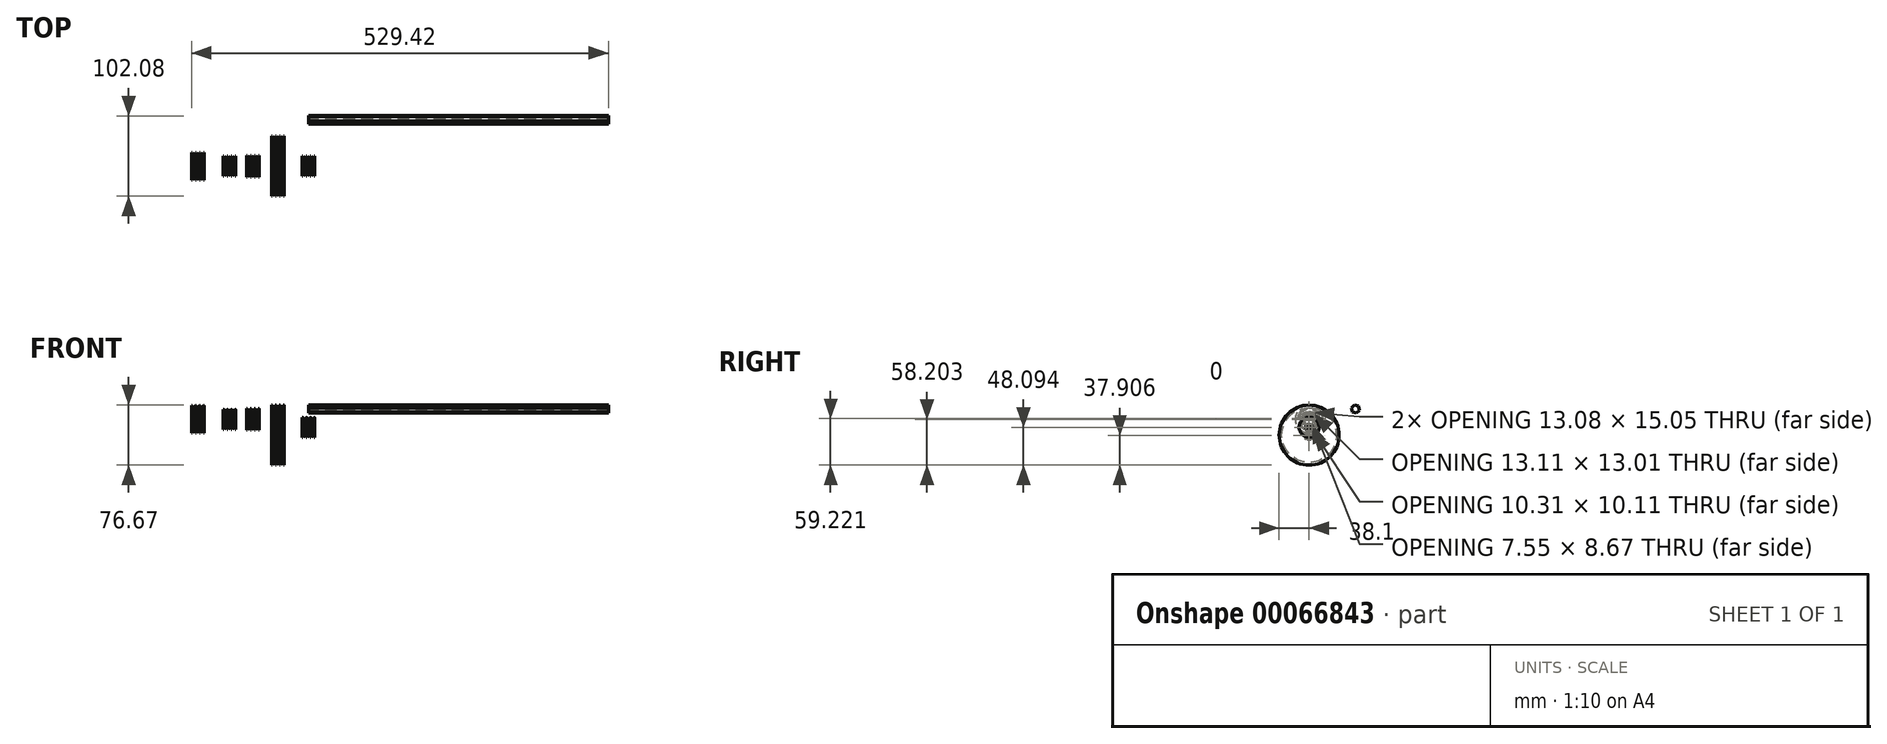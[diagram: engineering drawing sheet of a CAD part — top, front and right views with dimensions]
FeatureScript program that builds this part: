
annotation { "Feature Type Name" : "Feature", "Feature Type Description" : "" }
export const myFeature = defineFeature(function(context is Context, id is Id, definition is map)
    precondition{}
    {
        {
            var Q0;
            Q0=qCreatedBy(makeId("Right.planeOp"),FACE);
            var sketch = newSketch(context, id + "F0", { "sketchPlane" : qUnion([Q0])});
            skCircle(sketch, "E0.cCircle", {"center": v(58.72, 13.02) * mm, "radius": 4.76 * mm, "construction": true});
            skLineSegment(sketch, "E0.0", {"start": v(57.45, 18.37) * mm, "end": v(62.72, 16.79) * mm});
            skLineSegment(sketch, "E0.1", {"start": v(62.72, 16.79) * mm, "end": v(63.98, 11.43) * mm});
            skLineSegment(sketch, "E0.2", {"start": v(63.98, 11.43) * mm, "end": v(59.98, 7.66) * mm});
            skLineSegment(sketch, "E0.3", {"start": v(59.98, 7.66) * mm, "end": v(54.71, 9.24) * mm});
            skLineSegment(sketch, "E0.4", {"start": v(54.71, 9.24) * mm, "end": v(53.45, 14.6) * mm});
            skLineSegment(sketch, "E0.5", {"start": v(53.45, 14.6) * mm, "end": v(57.45, 18.37) * mm});
            skPoint(sketch, "E0.0.midPoint", {"position": v(60.08, 17.58) * mm});
            skSolve(sketch);
        }
        {
            var Q0;
            Q0=makeQuery(id+"F0.imprint","IMPRINT",FACE,{"disambiguationData":[TD([[makeQuery(id+"F0.imprint","IMPRINT",EDGE,{"derivedFrom":sQuery(id+"F0.wireOp",EDGE,"E0.0")}),-1.0]])]});
            extrude(context, id + "F1", {"entities" : qUnion([Q0]), "depth" : 381 * mm});
        }
        {
            var Q0;
            Q0=qCreatedBy(makeId("Front.planeOp"),FACE);
            var sketch = newSketch(context, id + "F2", { "sketchPlane" : qUnion([Q0])});
            skArc(sketch, "E1", {"start": v(-45.43, 15.85) * mm, "mid": v(-43.92, 14.73) * mm, "end": v(-42.4, 15.85) * mm});
            skLineSegment(sketch, "E2", {"start": v(-42.4, 15.85) * mm, "end": v(-41.76, 17.9) * mm});
            skLineSegment(sketch, "E3", {"start": v(-46.07, 17.9) * mm, "end": v(-45.43, 15.85) * mm});
            skArc(sketch, "E4.1.0.0", {"start": v(-40.35, 15.85) * mm, "mid": v(-38.84, 14.73) * mm, "end": v(-37.32, 15.85) * mm});
            skLineSegment(sketch, "E4.1.0.1", {"start": v(-37.32, 15.85) * mm, "end": v(-36.68, 17.9) * mm});
            skLineSegment(sketch, "E4.1.0.2", {"start": v(-40.99, 17.9) * mm, "end": v(-40.35, 15.85) * mm});
            skArc(sketch, "E4.2.0.0", {"start": v(-35.27, 15.85) * mm, "mid": v(-33.76, 14.73) * mm, "end": v(-32.24, 15.85) * mm});
            skLineSegment(sketch, "E4.2.0.1", {"start": v(-32.24, 15.85) * mm, "end": v(-31.6, 17.9) * mm});
            skLineSegment(sketch, "E4.2.0.2", {"start": v(-35.9, 17.9) * mm, "end": v(-35.27, 15.85) * mm});
            skLineSegment(sketch, "E5", {"start": v(-46.7, 17.9) * mm, "end": v(-46.07, 17.9) * mm});
            skLineSegment(sketch, "E6", {"start": v(-30.97, 17.9) * mm, "end": v(-30.97, -20.2) * mm});
            skLineSegment(sketch, "E7", {"start": v(-46.7, 17.9) * mm, "end": v(-46.7, -20.2) * mm});
            skLineSegment(sketch, "E8", {"start": v(-46.7, -20.2) * mm, "end": v(-30.97, -20.2) * mm});
            skLineSegment(sketch, "E9.trimOffspring", {"start": v(-31.6, 17.9) * mm, "end": v(-30.97, 17.9) * mm});
            skLineSegment(sketch, "E10.trimOffspring", {"start": v(-36.68, 17.9) * mm, "end": v(-35.9, 17.9) * mm});
            skLineSegment(sketch, "E11.trimOffspring", {"start": v(-41.76, 17.9) * mm, "end": v(-40.99, 17.9) * mm});
            skArc(sketch, "E12", {"start": v(-6.6, 0.44) * mm, "mid": v(-5.08, -0.68) * mm, "end": v(-3.56, 0.44) * mm});
            skLineSegment(sketch, "E13", {"start": v(-3.56, 0.44) * mm, "end": v(-2.93, 2.5) * mm});
            skLineSegment(sketch, "E14", {"start": v(-7.23, 2.5) * mm, "end": v(-6.6, 0.44) * mm});
            skArc(sketch, "E15.1.0.0", {"start": v(-1.52, 0.44) * mm, "mid": v(0, -0.68) * mm, "end": v(1.52, 0.44) * mm});
            skLineSegment(sketch, "E15.1.0.1", {"start": v(1.52, 0.44) * mm, "end": v(2.15, 2.5) * mm});
            skLineSegment(sketch, "E15.1.0.2", {"start": v(-2.15, 2.5) * mm, "end": v(-1.52, 0.44) * mm});
            skArc(sketch, "E15.2.0.0", {"start": v(3.56, 0.44) * mm, "mid": v(5.08, -0.68) * mm, "end": v(6.6, 0.44) * mm});
            skLineSegment(sketch, "E15.2.0.1", {"start": v(6.6, 0.44) * mm, "end": v(7.23, 2.5) * mm});
            skLineSegment(sketch, "E15.2.0.2", {"start": v(2.93, 2.5) * mm, "end": v(3.56, 0.44) * mm});
            skLineSegment(sketch, "E16", {"start": v(-7.87, 2.5) * mm, "end": v(-7.23, 2.5) * mm});
            skLineSegment(sketch, "E17", {"start": v(7.87, 2.5) * mm, "end": v(7.87, -10.2) * mm});
            skLineSegment(sketch, "E18", {"start": v(-7.87, 2.5) * mm, "end": v(-7.87, -10.2) * mm});
            skLineSegment(sketch, "E19", {"start": v(-7.87, -10.2) * mm, "end": v(7.87, -10.2) * mm});
            skLineSegment(sketch, "E20.trimOffspring", {"start": v(7.23, 2.5) * mm, "end": v(7.87, 2.5) * mm});
            skLineSegment(sketch, "E21.trimOffspring", {"start": v(2.15, 2.5) * mm, "end": v(2.93, 2.5) * mm});
            skLineSegment(sketch, "E22.trimOffspring", {"start": v(-2.93, 2.5) * mm, "end": v(-2.15, 2.5) * mm});
            skArc(sketch, "E23", {"start": v(-77.18, 11.44) * mm, "mid": v(-75.66, 10.32) * mm, "end": v(-74.15, 11.44) * mm});
            skLineSegment(sketch, "E24", {"start": v(-74.15, 11.44) * mm, "end": v(-73.51, 13.5) * mm});
            skLineSegment(sketch, "E25", {"start": v(-77.82, 13.5) * mm, "end": v(-77.18, 11.44) * mm});
            skArc(sketch, "E26.1.0.0", {"start": v(-72.1, 11.44) * mm, "mid": v(-70.58, 10.32) * mm, "end": v(-69.07, 11.44) * mm});
            skLineSegment(sketch, "E26.1.0.1", {"start": v(-69.07, 11.44) * mm, "end": v(-68.43, 13.5) * mm});
            skLineSegment(sketch, "E26.1.0.2", {"start": v(-72.74, 13.5) * mm, "end": v(-72.1, 11.44) * mm});
            skArc(sketch, "E26.2.0.0", {"start": v(-67.02, 11.44) * mm, "mid": v(-65.5, 10.32) * mm, "end": v(-63.99, 11.44) * mm});
            skLineSegment(sketch, "E26.2.0.1", {"start": v(-63.99, 11.44) * mm, "end": v(-63.35, 13.5) * mm});
            skLineSegment(sketch, "E26.2.0.2", {"start": v(-67.66, 13.5) * mm, "end": v(-67.02, 11.44) * mm});
            skLineSegment(sketch, "E27", {"start": v(-78.45, 13.5) * mm, "end": v(-77.82, 13.5) * mm});
            skLineSegment(sketch, "E28", {"start": v(-62.72, 13.5) * mm, "end": v(-62.72, 0) * mm});
            skLineSegment(sketch, "E29", {"start": v(-78.45, 13.5) * mm, "end": v(-78.45, 0) * mm});
            skLineSegment(sketch, "E30", {"start": v(-78.45, 0) * mm, "end": v(-62.72, 0) * mm});
            skLineSegment(sketch, "E31.trimOffspring", {"start": v(-63.35, 13.5) * mm, "end": v(-62.72, 13.5) * mm});
            skLineSegment(sketch, "E32.trimOffspring", {"start": v(-68.43, 13.5) * mm, "end": v(-67.66, 13.5) * mm});
            skLineSegment(sketch, "E33.trimOffspring", {"start": v(-73.51, 13.5) * mm, "end": v(-72.74, 13.5) * mm});
            skArc(sketch, "E34", {"start": v(-106.95, 10.64) * mm, "mid": v(-105.44, 9.52) * mm, "end": v(-103.92, 10.64) * mm});
            skLineSegment(sketch, "E35", {"start": v(-103.92, 10.64) * mm, "end": v(-103.28, 12.7) * mm});
            skLineSegment(sketch, "E36", {"start": v(-107.59, 12.7) * mm, "end": v(-106.95, 10.64) * mm});
            skArc(sketch, "E37.1.0.0", {"start": v(-101.87, 10.64) * mm, "mid": v(-100.36, 9.52) * mm, "end": v(-98.84, 10.64) * mm});
            skLineSegment(sketch, "E37.1.0.1", {"start": v(-98.84, 10.64) * mm, "end": v(-98.2, 12.7) * mm});
            skLineSegment(sketch, "E37.1.0.2", {"start": v(-102.5, 12.7) * mm, "end": v(-101.87, 10.64) * mm});
            skArc(sketch, "E37.2.0.0", {"start": v(-96.8, 10.64) * mm, "mid": v(-95.28, 9.53) * mm, "end": v(-93.76, 10.64) * mm});
            skLineSegment(sketch, "E37.2.0.1", {"start": v(-93.76, 10.64) * mm, "end": v(-93.12, 12.7) * mm});
            skLineSegment(sketch, "E37.2.0.2", {"start": v(-97.43, 12.7) * mm, "end": v(-96.8, 10.64) * mm});
            skLineSegment(sketch, "E38", {"start": v(-108.22, 12.7) * mm, "end": v(-107.59, 12.7) * mm});
            skLineSegment(sketch, "E39", {"start": v(-92.49, 12.7) * mm, "end": v(-92.49, 0) * mm});
            skLineSegment(sketch, "E40", {"start": v(-108.22, 12.7) * mm, "end": v(-108.22, 0) * mm});
            skLineSegment(sketch, "E41", {"start": v(-108.22, 0) * mm, "end": v(-92.49, 0) * mm});
            skLineSegment(sketch, "E42.trimOffspring", {"start": v(-93.12, 12.7) * mm, "end": v(-92.49, 12.7) * mm});
            skLineSegment(sketch, "E43.trimOffspring", {"start": v(-98.2, 12.7) * mm, "end": v(-97.43, 12.7) * mm});
            skLineSegment(sketch, "E44.trimOffspring", {"start": v(-103.28, 12.7) * mm, "end": v(-102.5, 12.7) * mm});
            skArc(sketch, "E45", {"start": v(-147.15, 15.4) * mm, "mid": v(-145.63, 14.29) * mm, "end": v(-144.11, 15.4) * mm});
            skLineSegment(sketch, "E46", {"start": v(-144.11, 15.4) * mm, "end": v(-143.48, 17.46) * mm});
            skLineSegment(sketch, "E47", {"start": v(-147.78, 17.46) * mm, "end": v(-147.15, 15.4) * mm});
            skArc(sketch, "E48.1.0.0", {"start": v(-142.07, 15.4) * mm, "mid": v(-140.55, 14.29) * mm, "end": v(-139.03, 15.4) * mm});
            skLineSegment(sketch, "E48.1.0.1", {"start": v(-139.03, 15.4) * mm, "end": v(-138.4, 17.46) * mm});
            skLineSegment(sketch, "E48.1.0.2", {"start": v(-142.7, 17.46) * mm, "end": v(-142.07, 15.4) * mm});
            skArc(sketch, "E48.2.0.0", {"start": v(-136.99, 15.4) * mm, "mid": v(-135.47, 14.29) * mm, "end": v(-133.95, 15.4) * mm});
            skLineSegment(sketch, "E48.2.0.1", {"start": v(-133.95, 15.4) * mm, "end": v(-133.32, 17.46) * mm});
            skLineSegment(sketch, "E48.2.0.2", {"start": v(-137.62, 17.46) * mm, "end": v(-136.99, 15.4) * mm});
            skLineSegment(sketch, "E49", {"start": v(-148.42, 17.46) * mm, "end": v(-147.78, 17.46) * mm});
            skLineSegment(sketch, "E50", {"start": v(-132.68, 17.46) * mm, "end": v(-132.68, 0) * mm});
            skLineSegment(sketch, "E51", {"start": v(-148.42, 17.46) * mm, "end": v(-148.42, 0) * mm});
            skLineSegment(sketch, "E52", {"start": v(-148.42, 0) * mm, "end": v(-132.68, 0) * mm});
            skLineSegment(sketch, "E53.trimOffspring", {"start": v(-133.32, 17.46) * mm, "end": v(-132.68, 17.46) * mm});
            skLineSegment(sketch, "E54.trimOffspring", {"start": v(-138.4, 17.46) * mm, "end": v(-137.62, 17.46) * mm});
            skLineSegment(sketch, "E55.trimOffspring", {"start": v(-143.48, 17.46) * mm, "end": v(-142.7, 17.46) * mm});
            skSolve(sketch);
        }
        {
            var Q0;
            Q0=makeQuery(id+"F2.imprint","IMPRINT",FACE,{"disambiguationData":[TD([[makeQuery(id+"F2.imprint","IMPRINT",EDGE,{"derivedFrom":sQuery(id+"F2.wireOp",EDGE,"E1")}),-1.0]])]});
            var Q1;
            Q1=sQuery(id+"F2.wireOp",EDGE,"E8");
            revolve(context, id + "F3", {"entities" : qUnion([Q0]), "axis" : qUnion([Q1]), "revolveType" : RevolveType.FULL});
        }
        {
            var Q0;
            Q0=makeQuery(id+"F2.imprint","IMPRINT",FACE,{"disambiguationData":[TD([[makeQuery(id+"F2.imprint","IMPRINT",EDGE,{"derivedFrom":sQuery(id+"F2.wireOp",EDGE,"E12")}),-1.0]])]});
            var Q1;
            Q1=sQuery(id+"F2.wireOp",EDGE,"E19");
            revolve(context, id + "F4", {"entities" : qUnion([Q0]), "axis" : qUnion([Q1]), "revolveType" : RevolveType.FULL});
        }
        {
            var Q0;
            Q0=makeQuery(id+"F4.opRevolve","SWEPT_FACE",FACE,{"disambiguationData":[OSD([sQuery(id+"F2.wireOp",EDGE,"E17")])]});
            var sketch = newSketch(context, id + "F5", { "sketchPlane" : qUnion([Q0])});
            skCircle(sketch, "E56.cCircle", {"center": v(0, -10.2) * mm, "radius": 3.75 * mm, "construction": true});
            skLineSegment(sketch, "E56.0", {"start": v(-0.05, -5.87) * mm, "end": v(3.73, -8) * mm});
            skLineSegment(sketch, "E56.1", {"start": v(3.73, -8) * mm, "end": v(3.78, -12.33) * mm});
            skLineSegment(sketch, "E56.2", {"start": v(3.78, -12.33) * mm, "end": v(0.05, -14.54) * mm});
            skLineSegment(sketch, "E56.3", {"start": v(0.05, -14.54) * mm, "end": v(-3.73, -12.41) * mm});
            skLineSegment(sketch, "E56.4", {"start": v(-3.73, -12.41) * mm, "end": v(-3.78, -8.08) * mm});
            skLineSegment(sketch, "E56.5", {"start": v(-3.78, -8.08) * mm, "end": v(-0.05, -5.87) * mm});
            skPoint(sketch, "E56.0.midPoint", {"position": v(1.84, -6.93) * mm});
            skSolve(sketch);
        }
        {
            var Q0;
            Q0=makeQuery(id+"F5.imprint","IMPRINT",FACE,{"disambiguationData":[TD([[makeQuery(id+"F5.imprint","IMPRINT",EDGE,{"derivedFrom":sQuery(id+"F5.wireOp",EDGE,"E56.0")}),-1.0]])]});
            extrude(context, id + "F6", {"entities" : qUnion([Q0]), "operationType" : NewBodyOperationType.REMOVE, "oppositeDirection" : true, "depth" : 25.4 * mm});
        }
        {
            var Q0;
            Q0=makeQuery(id+"F3.opRevolve","SWEPT_FACE",FACE,{"disambiguationData":[OSD([sQuery(id+"F2.wireOp",EDGE,"E6")])]});
            var sketch = newSketch(context, id + "F7", { "sketchPlane" : qUnion([Q0])});
            skArc(sketch, "E57", {"start": v(-2, -15.34) * mm, "mid": v(0, -25.45) * mm, "end": v(2, -15.34) * mm});
            skLineSegment(sketch, "E58.top", {"start": v(-2, -17.2) * mm, "end": v(2, -17.2) * mm});
            skLineSegment(sketch, "E58.left", {"start": v(-2, -15.34) * mm, "end": v(-2, -17.2) * mm});
            skLineSegment(sketch, "E58.right", {"start": v(2, -15.34) * mm, "end": v(2, -17.2) * mm});
            skPoint(sketch, "E59.orphan", {"position": v(2, -15.2) * mm});
            skSolve(sketch);
        }
        {
            var Q0;
            Q0 = qSketchRegion(id + "F7", true);
            extrude(context, id + "F8", {"entities" : qUnion([Q0]), "operationType" : NewBodyOperationType.REMOVE, "oppositeDirection" : true, "depth" : 25.4 * mm});
        }
        {
            var Q0;
            Q0=makeQuery(id+"F2.imprint","IMPRINT",FACE,{"disambiguationData":[TD([[makeQuery(id+"F2.imprint","IMPRINT",EDGE,{"derivedFrom":sQuery(id+"F2.wireOp",EDGE,"E23")}),-1.0]])]});
            var Q1;
            Q1=makeQuery(id+"F2.imprint","IMPRINT",FACE,{"disambiguationData":[TD([[makeQuery(id+"F2.imprint","IMPRINT",EDGE,{"derivedFrom":sQuery(id+"F2.wireOp",EDGE,"E34")}),-1.0]])]});
            var Q2;
            Q2=sQuery(id+"F2.wireOp",EDGE,"E30");
            revolve(context, id + "F9", {"entities" : qUnion([Q0, Q1]), "axis" : qUnion([Q2]), "revolveType" : RevolveType.FULL});
        }
        {
            var Q0;
            Q0=makeQuery(id+"F9.opRevolve","SWEPT_FACE",FACE,{"disambiguationData":[OSD([sQuery(id+"F2.wireOp",EDGE,"E28")])]});
            var sketch = newSketch(context, id + "F10", { "sketchPlane" : qUnion([Q0])});
            skCircle(sketch, "E60", {"center": v(0, 0) * mm, "radius": 6.6 * mm});
            skLineSegment(sketch, "E61.bottom", {"start": v(-1.84, 8.45) * mm, "end": v(1.84, 8.45) * mm});
            skLineSegment(sketch, "E61.top", {"start": v(-1.84, 4.76) * mm, "end": v(1.84, 4.76) * mm});
            skLineSegment(sketch, "E61.left", {"start": v(-1.84, 8.45) * mm, "end": v(-1.84, 4.76) * mm});
            skLineSegment(sketch, "E61.right", {"start": v(1.84, 8.45) * mm, "end": v(1.84, 4.76) * mm});
            skPoint(sketch, "E62", {"position": v(0, 4.76) * mm});
            skSolve(sketch);
        }
        {
            var Q0;
            Q0 = qSketchRegion(id + "F10", true);
            extrude(context, id + "F11", {"entities" : qUnion([Q0]), "operationType" : NewBodyOperationType.REMOVE, "endBound" : BoundingType.THROUGH_ALL, "oppositeDirection" : true, "depth" : 25.4 * mm});
        }
        {
            var Q0;
            Q0=makeQuery(id+"F9.opRevolve","SWEPT_FACE",FACE,{"disambiguationData":[OSD([sQuery(id+"F2.wireOp",EDGE,"E39")])]});
            var sketch = newSketch(context, id + "F12", { "sketchPlane" : qUnion([Q0])});
            skCircle(sketch, "E63.cCircle", {"center": v(0, 0) * mm, "radius": 5.02 * mm, "construction": true});
            skLineSegment(sketch, "E63.0", {"start": v(-2.9, 5.02) * mm, "end": v(2.9, 5.02) * mm});
            skLineSegment(sketch, "E63.1", {"start": v(2.9, 5.02) * mm, "end": v(5.8, 0) * mm});
            skLineSegment(sketch, "E63.2", {"start": v(5.8, 0) * mm, "end": v(2.9, -5.02) * mm});
            skLineSegment(sketch, "E63.3", {"start": v(2.9, -5.02) * mm, "end": v(-2.9, -5.02) * mm});
            skLineSegment(sketch, "E63.4", {"start": v(-2.9, -5.02) * mm, "end": v(-5.8, 0) * mm});
            skLineSegment(sketch, "E63.5", {"start": v(-5.8, 0) * mm, "end": v(-2.9, 5.02) * mm});
            skPoint(sketch, "E63.0.midPoint", {"position": v(0, 5.02) * mm});
            skSolve(sketch);
        }
        {
            var Q0;
            Q0 = qSketchRegion(id + "F12", true);
            extrude(context, id + "F13", {"entities" : qUnion([Q0]), "operationType" : NewBodyOperationType.REMOVE, "endBound" : BoundingType.THROUGH_ALL, "oppositeDirection" : true, "depth" : 25.4 * mm});
        }
        {
            var Q0;
            Q0=makeQuery(id+"F2.imprint","IMPRINT",FACE,{"disambiguationData":[TD([[makeQuery(id+"F2.imprint","IMPRINT",EDGE,{"derivedFrom":sQuery(id+"F2.wireOp",EDGE,"E45")}),-1.0]])]});
            var Q1;
            Q1=sQuery(id+"F2.wireOp",EDGE,"E52");
            revolve(context, id + "F14", {"entities" : qUnion([Q0]), "axis" : qUnion([Q1]), "revolveType" : RevolveType.FULL});
        }
        {
            var Q0;
            Q0=makeQuery(id+"F14.opRevolve","SWEPT_FACE",FACE,{"disambiguationData":[OSD([sQuery(id+"F2.wireOp",EDGE,"E50")])]});
            var sketch = newSketch(context, id + "F15", { "sketchPlane" : qUnion([Q0])});
            skCircle(sketch, "E64", {"center": v(0, 0) * mm, "radius": 6.6 * mm});
            skLineSegment(sketch, "E65.bottom", {"start": v(-1.59, 8.2) * mm, "end": v(1.59, 8.2) * mm});
            skLineSegment(sketch, "E65.top", {"start": v(-1.59, 5.02) * mm, "end": v(1.59, 5.02) * mm});
            skLineSegment(sketch, "E65.left", {"start": v(-1.59, 8.2) * mm, "end": v(-1.59, 5.02) * mm});
            skLineSegment(sketch, "E65.right", {"start": v(1.59, 8.2) * mm, "end": v(1.59, 5.02) * mm});
            skPoint(sketch, "E66", {"position": v(0, 5.02) * mm});
            skSolve(sketch);
        }
        {
            var Q0;
            {var subQ5=sQuery(id+"F15.wireOp",EDGE,"E65.top");Q0=makeQuery(id+"F15.imprint","IMPRINT",FACE,{"disambiguationData":[TD([[makeQuery(id+"F15.imprint","IMPRINT",EDGE,{"derivedFrom":subQ5}),-1.0]])]});}
            extrude(context, id + "F16", {"entities" : qUnion([Q0]), "operationType" : NewBodyOperationType.REMOVE, "endBound" : BoundingType.THROUGH_ALL, "oppositeDirection" : true, "depth" : 25.4 * mm});
        }
    });
